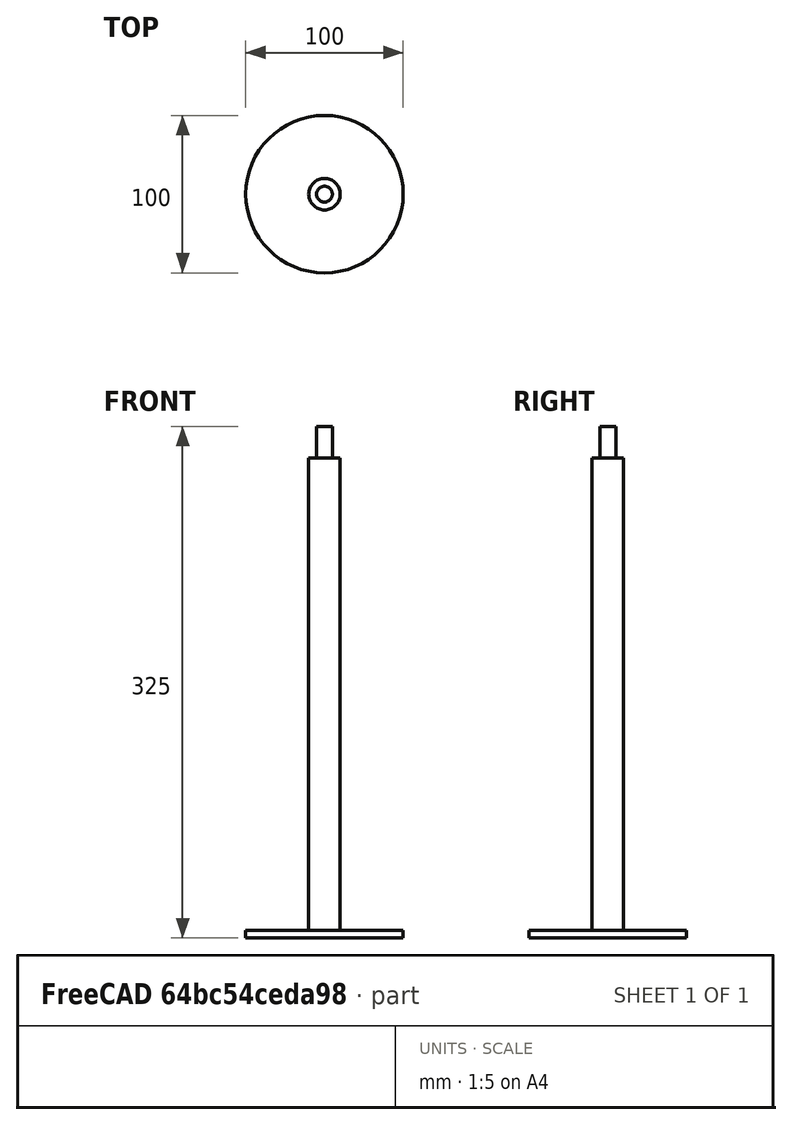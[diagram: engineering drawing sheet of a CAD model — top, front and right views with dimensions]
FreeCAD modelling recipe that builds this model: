
FCSTD DOCUMENT  (FreeCAD 0.19R24291 (Git))
Label: Tart_leg
License: All rights reserved
LicenseURL: http://en.wikipedia.org/wiki/All_rights_reserved
objects: Sketcher::SketchObject×1, PartDesign::Revolution×1, PartDesign::Body×1
note: 4 computed .brp shape members not serialized (recipe doc carries the construction recipe); baked Part::Feature solids carry a one-line shape summary decoded from their .brp

FEATURE [Sketcher::SketchObject] Sketch
  FullyConstrained = true
  MapMode = 5
  Placement = pos=(0,0,0) rot=(1,0,0;1.5708rad)
  Support = -> [XZ_Plane]
  sketch-geometry (8):
    g0: LineSegment StartX=0 StartY=0 StartZ=0 EndX=-50 EndY=0 EndZ=0
    g1: LineSegment StartX=-50 StartY=0 StartZ=0 EndX=-50 EndY=5 EndZ=0
    g2: LineSegment StartX=-50 StartY=5 StartZ=0 EndX=-10 EndY=5 EndZ=0
    g3: LineSegment StartX=-10 StartY=5 StartZ=0 EndX=-10 EndY=305 EndZ=0
    g4: LineSegment StartX=-10 StartY=305 StartZ=0 EndX=-5 EndY=305 EndZ=0
    g5: LineSegment StartX=-5 StartY=305 StartZ=0 EndX=-5 EndY=325 EndZ=0
    g6: LineSegment StartX=-5 StartY=325 StartZ=0 EndX=0 EndY=325 EndZ=0
    g7: LineSegment StartX=0 StartY=325 StartZ=0 EndX=0 EndY=0 EndZ=0
  constraints (23):
    c: Coincident(g0,g-1)
    c: Horizontal(g0)
    c: Coincident(g1,g0)
    c: DistanceX(g0,g0) = 50
    c: Perpendicular(g1,g0)
    c: DistanceY(g1,g1) = 5
    c: Coincident(g2,g1)
    c: Horizontal(g2)
    c: DistanceX(g2,g2) = 40
    c: Coincident(g3,g2)
    c: Vertical(g3)
    c: DistanceY(g3,g3) = 300
    c: Coincident(g4,g3)
    c: Perpendicular(g4,g3)
    c: DistanceX(g4,g4) = 5
    c: Coincident(g5,g4)
    c: Vertical(g5)
    c: DistanceY(g5,g5) = 20
    c: Coincident(g6,g5)
    c: PointOnObject(g6,g-2)
    c: Horizontal(g6)
    c: Coincident(g7,g6)
    c: Coincident(g7,g0)
FEATURE [PartDesign::Revolution] Revolution
  Angle = 360
  Axis = (0,2e-16,1)
  Base = (0,0,0)
  Placement = pos=(0,0,0) rot=(1,0,0;1.5708rad)
  Profile = -> Sketch
  ReferenceAxis = -> Sketch [V_Axis]
FEATURE [PartDesign::Body] Body
  Group = -> [Sketch,Revolution]
  Origin = -> Origin
  Tip = -> Revolution
